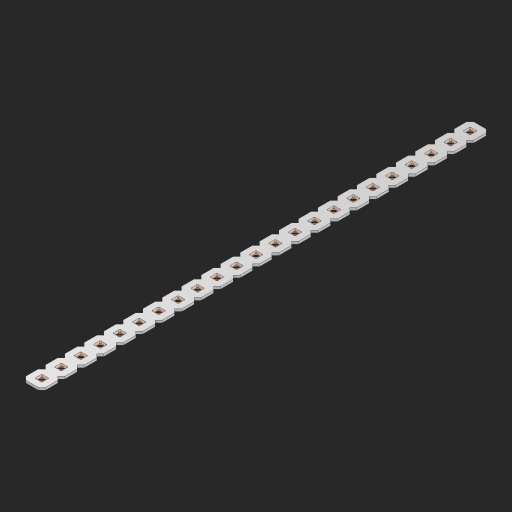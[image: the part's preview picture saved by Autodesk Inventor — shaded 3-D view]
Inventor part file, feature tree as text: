
AUTODESK INVENTOR PART (.ipt)
format: ipt  version: 2023 (Build 270158000, 158)  size: 525,824 bytes
history: native  units: in
note: dims shown in document units (in); Inventor stores cm internally (conversion verified against a paired STEP export)
features: other x24, extrude x22, sketch x2, pattern_linear x1
ambient origin geometry x8: Origin, YZ Plane, XZ Plane, XY Plane, X Axis, Y Axis, Z Axis, Center Point
bodies: Solid1 (feature_tree), Body (feature_tree)
feature tree (49):
  pattern_linear  "Rectangular Pattern1"  Spacing1=0.09in  [1 undecoded]
  sketch  "Sketch1"  dims[d1=0.5in]
  sketch  "Sketch2"  dims[d2=0.182in d3=0.09in d4=0.09in d5=0.09in d6=0.09in d7=0.09in d8=0.09in d9=0.09in d10=0.09in d11=0.02in d13=0.0in d14=0.172in d15=0.0625in d16=0.0in d19=0.5in d22=0.5in]
  other  "Srf1"
  other  "Srf126"
  other  "Srf127"
  other  "Srf128"
  other  "Srf129"
  other  "Srf130"
  other  "Srf131"
  other  "Srf250"
  other  "Srf251"
  other  "Srf252"
  other  "Srf253"
  other  "Srf254"
  other  "Srf255"
  other  "Srf256"
  other  "Srf257"
  other  "Srf258"
  other  "Srf259"
  other  "Srf260"
  other  "Srf261"
  other  "Srf262"
  other  "Srf263"
  other  "Srf264"
  other  "Srf265"
  other  "Circle"
  extrude  "ExtrusionSrf126"  Depth=0.09in
  extrude  "ExtrusionSrf127"  Depth=0.09in
  extrude  "ExtrusionSrf128"  Depth=0.09in
  extrude  "ExtrusionSrf129"  Depth=0.09in
  extrude  "ExtrusionSrf130"  Depth=0.09in
  extrude  "ExtrusionSrf131"  Depth=0.09in
  extrude  "ExtrusionSrf250"  Depth=0.09in
  extrude  "ExtrusionSrf251"  Depth=0.02in
  extrude  "ExtrusionSrf252"  TaperAngle=0.0deg  [1 undecoded]
  extrude  "ExtrusionSrf253"  Depth=0.5in
  extrude  "ExtrusionSrf254"  Depth=0.0625in TaperAngle=0.0deg
  extrude  "ExtrusionSrf255"  Depth=0.5in
  extrude  "ExtrusionSrf256"  Depth=0.5in
  extrude  "ExtrusionSrf257"  [1 undecoded]
  extrude  "ExtrusionSrf258"  [1 undecoded]
  extrude  "ExtrusionSrf259"  [1 undecoded]
  extrude  "ExtrusionSrf260"  [1 undecoded]
  extrude  "ExtrusionSrf261"  [1 undecoded]
  extrude  "ExtrusionSrf262"  [1 undecoded]
  extrude  "ExtrusionSrf263"  [1 undecoded]
  extrude  "ExtrusionSrf264"  [1 undecoded]
  extrude  "ExtrusionSrf265"  [1 undecoded]
note: 11 required parameter values undecoded (feature->parameter linkage not recoverable at this tier; creation-order binding heuristic only, values carry confidence <= 0.55)
